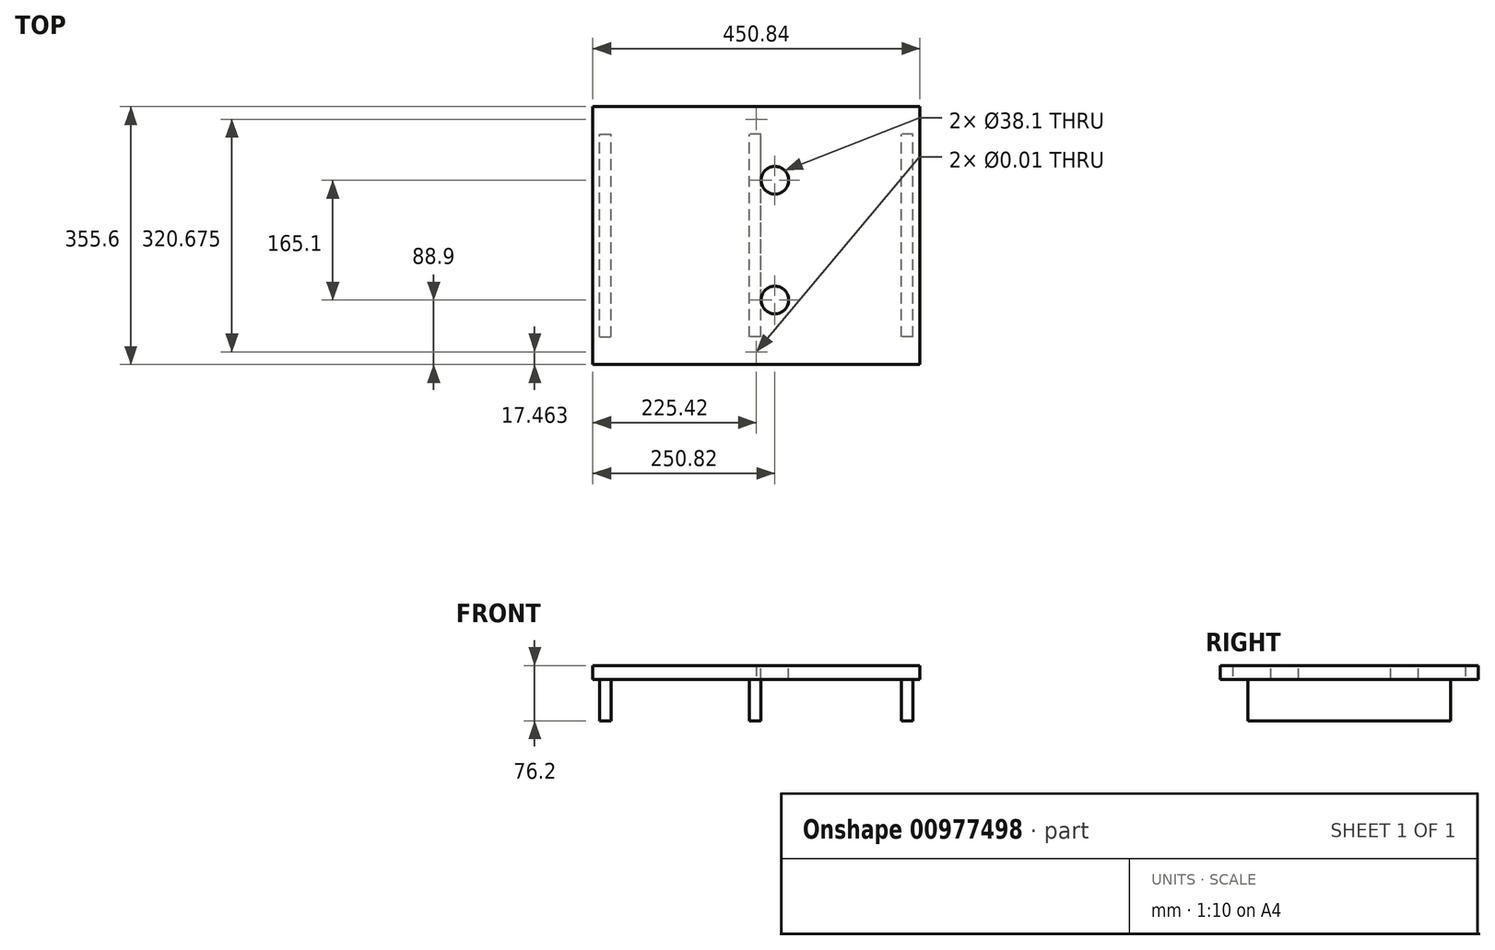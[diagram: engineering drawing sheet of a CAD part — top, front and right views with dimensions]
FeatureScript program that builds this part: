
annotation { "Feature Type Name" : "Feature", "Feature Type Description" : "" }
export const myFeature = defineFeature(function(context is Context, id is Id, definition is map)
    precondition{}
    {
        {
            var Q0;
            Q0=qCreatedBy(makeId("Top.planeOp"),FACE);
            var sketch = newSketch(context, id + "F0", { "sketchPlane" : qUnion([Q0])});
            skLineSegment(sketch, "E0.bottom", {"start": v(-225.42, 177.8) * mm, "end": v(225.43, 177.8) * mm});
            skLineSegment(sketch, "E0.top", {"start": v(-225.43, -177.8) * mm, "end": v(225.42, -177.8) * mm});
            skLineSegment(sketch, "E0.left", {"start": v(-225.42, 177.8) * mm, "end": v(-225.43, -177.8) * mm});
            skLineSegment(sketch, "E0.right", {"start": v(225.43, 177.8) * mm, "end": v(225.42, -177.8) * mm});
            skPoint(sketch, "E0.middle", {"position": v(0, 0) * mm});
            skSolve(sketch);
        }
        {
            var Q0;
            Q0=makeQuery(id+"F0.imprint","IMPRINT",FACE,{"disambiguationData":[TD([[makeQuery(id+"F0.imprint","IMPRINT",EDGE,{"derivedFrom":sQuery(id+"F0.wireOp",EDGE,"E0.bottom")}),-1.0]])]});
            extrude(context, id + "F1", {"entities" : qUnion([Q0]), "depth" : 19.05 * mm, "offsetDistance" : 25 * mm});
        }
        {
            var Q0;
            Q0=makeQuery(id+"F1.opExtrude","CAP_FACE",FACE,{"disambiguationData":[OSD([sQuery(id+"F0.wireOp",EDGE,"E0.bottom"),sQuery(id+"F0.wireOp",EDGE,"E0.top"),sQuery(id+"F0.wireOp",EDGE,"E0.left"),sQuery(id+"F0.wireOp",EDGE,"E0.right")])],"isStart":false});
            var sketch = newSketch(context, id + "F2", { "sketchPlane" : qUnion([Q0])});
            skLineSegment(sketch, "E1.bottom", {"start": v(-200.03, 152.4) * mm, "end": v(98.43, 152.4) * mm});
            skLineSegment(sketch, "E1.top", {"start": v(-200.03, 12.7) * mm, "end": v(98.43, 12.7) * mm});
            skLineSegment(sketch, "E1.left", {"start": v(-200.02, 152.4) * mm, "end": v(-200.02, 12.7) * mm});
            skLineSegment(sketch, "E1.right", {"start": v(98.43, 152.4) * mm, "end": v(98.43, 12.7) * mm});
            skPoint(sketch, "E2", {"position": v(25.4, 76.2) * mm});
            skCircle(sketch, "E3", {"center": v(25.4, 76.2) * mm, "radius": 19.05 * mm});
            skLineSegment(sketch, "E4.bottom", {"start": v(-200.02, -12.7) * mm, "end": v(98.43, -12.7) * mm});
            skLineSegment(sketch, "E4.top", {"start": v(-200.02, -152.4) * mm, "end": v(98.43, -152.4) * mm});
            skLineSegment(sketch, "E4.left", {"start": v(-200.03, -12.7) * mm, "end": v(-200.03, -152.4) * mm});
            skLineSegment(sketch, "E4.right", {"start": v(98.43, -12.7) * mm, "end": v(98.43, -152.4) * mm});
            skCircle(sketch, "E5", {"center": v(25.4, -88.9) * mm, "radius": 19.05 * mm});
            skSolve(sketch);
        }
        {
            var Q0;
            Q0=sQuery(id+"F2.wireOp",VERTEX,"E2");
            var Q1;
            Q1=sQuery(id+"F2.wireOp",VERTEX,"E5.center");
            var Q2;
            Q2=makeQuery(id+"F1.opExtrude","SWEPT_BODY",BODY,{"disambiguationData":[OSD([sQuery(id+"F0.wireOp",EDGE,"E0.bottom"),sQuery(id+"F0.wireOp",EDGE,"E0.top"),sQuery(id+"F0.wireOp",EDGE,"E0.left"),sQuery(id+"F0.wireOp",EDGE,"E0.right")])]});
            hole(context, id + "F3", {"style" : HoleStyle.SIMPLE, "endStyle" : HoleEndStyle.THROUGH, "holeDiameter" : 38.1 * mm, "majorDiameter" : 5 * mm, "isTappedThrough" : true, "tappedDepth" : 7 * mm, "tapClearance" : 3, "startFromSketch" : true, "locations" : qUnion([Q0, Q1]), "scope" : qUnion([Q2])});
        }
        {
            var Q0;
            Q0=makeQuery(id+"F1.opExtrude","CAP_FACE",FACE,{"disambiguationData":[OSD([sQuery(id+"F0.wireOp",EDGE,"E0.bottom"),sQuery(id+"F0.wireOp",EDGE,"E0.top"),sQuery(id+"F0.wireOp",EDGE,"E0.left"),sQuery(id+"F0.wireOp",EDGE,"E0.right")])],"isStart":true});
            var sketch = newSketch(context, id + "F4", { "sketchPlane" : qUnion([Q0])});
            skPoint(sketch, "E6", {"position": v(0, -160.34) * mm});
            skPoint(sketch, "E7", {"position": v(0, 160.34) * mm});
            skSolve(sketch);
        }
        {
            var Q0;
            Q0=sQuery(id+"F4.wireOp",VERTEX,"E7");
            var Q1;
            Q1=sQuery(id+"F4.wireOp",VERTEX,"E6");
            var Q2;
            Q2=makeQuery(id+"F1.opExtrude","SWEPT_BODY",BODY,{"disambiguationData":[OSD([sQuery(id+"F0.wireOp",EDGE,"E0.bottom"),sQuery(id+"F0.wireOp",EDGE,"E0.top"),sQuery(id+"F0.wireOp",EDGE,"E0.left"),sQuery(id+"F0.wireOp",EDGE,"E0.right")])]});
            hole(context, id + "F5", {"style" : HoleStyle.SIMPLE, "endStyle" : HoleEndStyle.THROUGH, "holeDiameter" : 3 / 203.2 * mm, "majorDiameter" : 5 * mm, "isTappedThrough" : true, "tappedDepth" : 7 * mm, "tapClearance" : 3, "startFromSketch" : true, "locations" : qUnion([Q0, Q1]), "scope" : qUnion([Q2])});
        }
        {
            var Q0;
            Q0=qCreatedBy(makeId("Front.planeOp"),FACE);
            var sketch = newSketch(context, id + "F6", { "sketchPlane" : qUnion([Q0])});
            skLineSegment(sketch, "E8.bottom", {"start": v(6.35, 0) * mm, "end": v(-9.52, 0) * mm});
            skLineSegment(sketch, "E8.top", {"start": v(6.35, -57.15) * mm, "end": v(-9.52, -57.15) * mm});
            skLineSegment(sketch, "E8.left", {"start": v(6.35, 0) * mm, "end": v(6.35, -57.15) * mm});
            skLineSegment(sketch, "E8.right", {"start": v(-9.52, 0) * mm, "end": v(-9.52, -57.15) * mm});
            skPoint(sketch, "E9", {"position": v(-1.59, 0) * mm});
            skLineSegment(sketch, "E10.bottom", {"start": v(215.9, 0) * mm, "end": v(200.03, 0) * mm});
            skLineSegment(sketch, "E10.top", {"start": v(215.9, -57.15) * mm, "end": v(200.03, -57.15) * mm});
            skLineSegment(sketch, "E10.left", {"start": v(215.9, 0) * mm, "end": v(215.9, -57.15) * mm});
            skLineSegment(sketch, "E10.right", {"start": v(200.03, 0) * mm, "end": v(200.03, -57.15) * mm});
            skLineSegment(sketch, "E11.bottom", {"start": v(-215.9, 0) * mm, "end": v(-200.02, 0) * mm});
            skLineSegment(sketch, "E11.top", {"start": v(-215.9, -57.15) * mm, "end": v(-200.02, -57.15) * mm});
            skLineSegment(sketch, "E11.left", {"start": v(-215.9, 0) * mm, "end": v(-215.9, -57.15) * mm});
            skLineSegment(sketch, "E11.right", {"start": v(-200.02, 0) * mm, "end": v(-200.02, -57.15) * mm});
            skSolve(sketch);
        }
        {
            var Q0;
            Q0=makeQuery(id+"F6.imprint","IMPRINT",FACE,{"disambiguationData":[TD([[makeQuery(id+"F6.imprint","IMPRINT",EDGE,{"derivedFrom":sQuery(id+"F6.wireOp",EDGE,"E10.bottom")}),1.0]])]});
            var Q1;
            Q1=makeQuery(id+"F6.imprint","IMPRINT",FACE,{"disambiguationData":[TD([[makeQuery(id+"F6.imprint","IMPRINT",EDGE,{"derivedFrom":sQuery(id+"F6.wireOp",EDGE,"E8.bottom")}),1.0]])]});
            var Q2;
            Q2=makeQuery(id+"F6.imprint","IMPRINT",FACE,{"disambiguationData":[TD([[makeQuery(id+"F6.imprint","IMPRINT",EDGE,{"derivedFrom":sQuery(id+"F6.wireOp",EDGE,"E11.bottom")}),-1.0]])]});
            extrude(context, id + "F7", {"entities" : qUnion([Q0, Q1, Q2]), "operationType" : NewBodyOperationType.ADD, "depth" : 279.4 * mm, "offsetDistance" : 25 * mm, "symmetric" : true});
        }
    });
